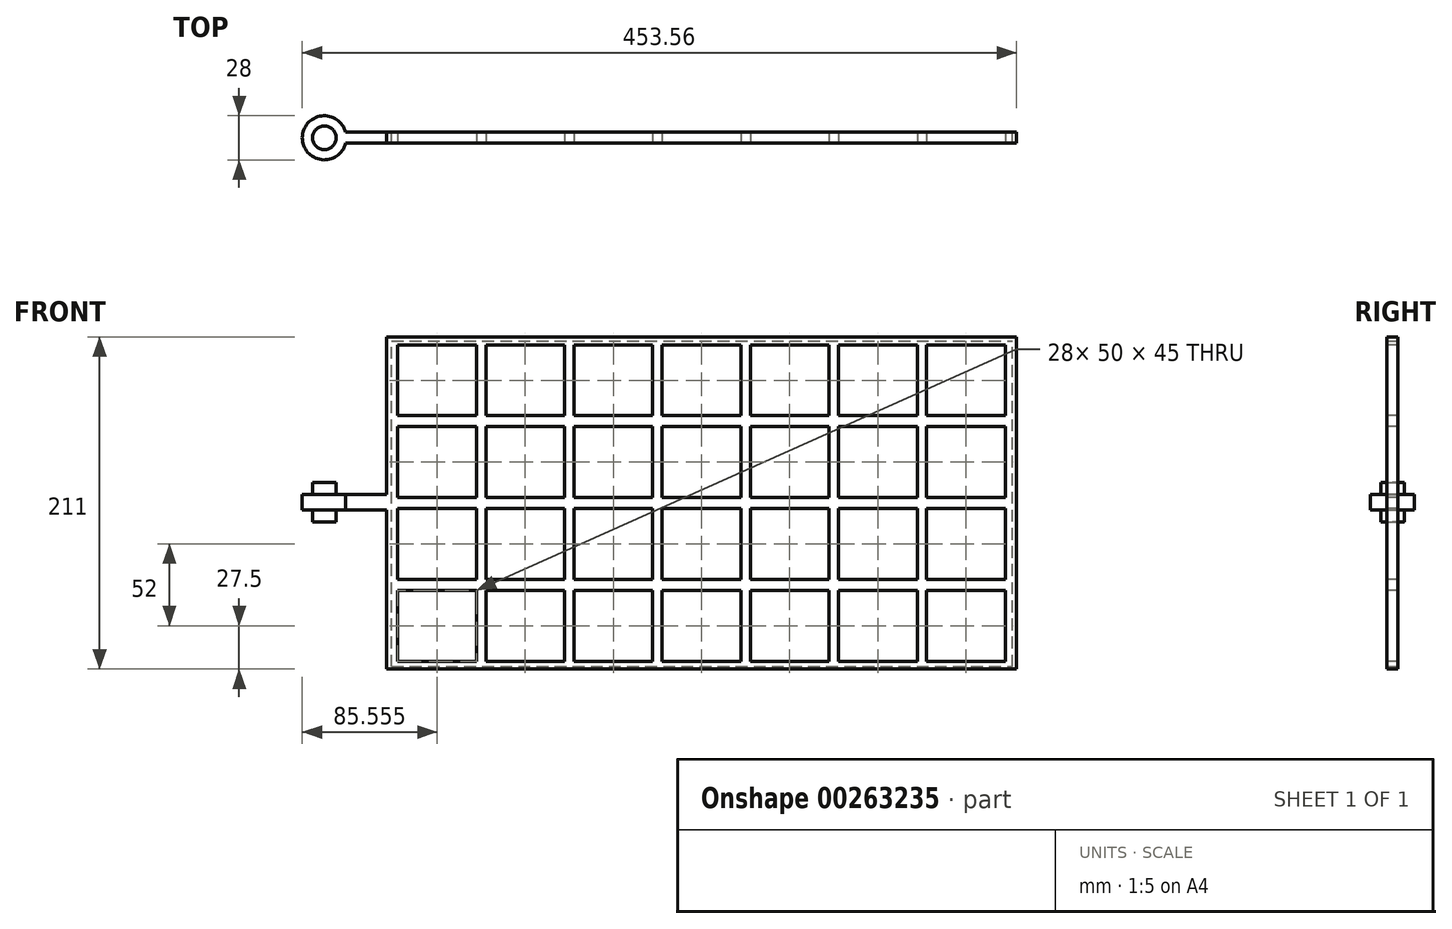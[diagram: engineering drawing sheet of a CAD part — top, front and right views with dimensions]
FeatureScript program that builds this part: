
annotation { "Feature Type Name" : "Feature", "Feature Type Description" : "" }
export const myFeature = defineFeature(function(context is Context, id is Id, definition is map)
    precondition{}
    {
        {
            var Q0;
            Q0=qCreatedBy(makeId("Top.planeOp"),FACE);
            var sketch = newSketch(context, id + "F0", { "sketchPlane" : qUnion([Q0])});
            skCircle(sketch, "E0", {"center": v(0, 0) * mm, "radius": 7.5 * mm});
            skSolve(sketch);
        }
        {
            var Q0;
            Q0 = qSketchRegion(id + "F0", true);
            extrude(context, id + "F1", {"entities" : qUnion([Q0]), "endBound" : BoundingType.SYMMETRIC, "depth" : 25 * mm});
        }
        {
            var Q0;
            Q0=qCreatedBy(makeId("Top.planeOp"),FACE);
            var sketch = newSketch(context, id + "F2", { "sketchPlane" : qUnion([Q0])});
            skArc(sketch, "E1", {"start": v(13.56, 3.5) * mm, "mid": v(-14, 0) * mm, "end": v(13.56, -3.5) * mm});
            skLineSegment(sketch, "E2", {"start": v(0, 0) * mm, "end": v(45.4, 0) * mm, "construction": true});
            skLineSegment(sketch, "E3.0", {"start": v(13.56, 3.5) * mm, "end": v(39.56, 3.5) * mm});
            skLineSegment(sketch, "E4.0", {"start": v(13.56, -3.5) * mm, "end": v(39.56, -3.5) * mm});
            skLineSegment(sketch, "E5", {"start": v(39.56, 3.5) * mm, "end": v(39.56, -3.5) * mm});
            skSolve(sketch);
        }
        {
            var Q0;
            Q0 = qSketchRegion(id + "F2", true);
            extrude(context, id + "F3", {"entities" : qUnion([Q0]), "operationType" : NewBodyOperationType.ADD, "endBound" : BoundingType.SYMMETRIC, "depth" : 10 * mm});
        }
        {
            var Q0;
            Q0=qCreatedBy(makeId("Front.planeOp"),FACE);
            var sketch = newSketch(context, id + "F4", { "sketchPlane" : qUnion([Q0])});
            skPoint(sketch, "E6", {"position": v(39.56, 0) * mm});
            skLineSegment(sketch, "E7", {"start": v(39.56, 5) * mm, "end": v(39.56, 105) * mm});
            skLineSegment(sketch, "E8", {"start": v(39.56, -5) * mm, "end": v(39.56, -106) * mm});
            skLineSegment(sketch, "E9", {"start": v(39.56, 105) * mm, "end": v(439.56, 105) * mm});
            skLineSegment(sketch, "E10", {"start": v(39.56, -106) * mm, "end": v(439.56, -106) * mm});
            skLineSegment(sketch, "E11", {"start": v(439.56, -106) * mm, "end": v(439.56, 105) * mm});
            skLineSegment(sketch, "E12", {"start": v(39.56, 5) * mm, "end": v(39.56, -5) * mm});
            skLineSegment(sketch, "E13.bottom", {"start": v(46.56, 100) * mm, "end": v(96.56, 100) * mm});
            skLineSegment(sketch, "E13.top", {"start": v(46.56, 55) * mm, "end": v(96.56, 55) * mm});
            skLineSegment(sketch, "E13.left", {"start": v(46.56, 100) * mm, "end": v(46.56, 55) * mm});
            skLineSegment(sketch, "E13.right", {"start": v(96.56, 100) * mm, "end": v(96.56, 55) * mm});
            skLineSegment(sketch, "E14.0.1.0", {"start": v(46.56, 3) * mm, "end": v(96.56, 3) * mm});
            skLineSegment(sketch, "E14.0.1.1", {"start": v(96.56, 48) * mm, "end": v(96.56, 3) * mm});
            skLineSegment(sketch, "E14.0.1.2", {"start": v(46.56, 48) * mm, "end": v(46.56, 3) * mm});
            skLineSegment(sketch, "E14.0.1.3", {"start": v(46.56, 48) * mm, "end": v(96.56, 48) * mm});
            skLineSegment(sketch, "E14.0.2.0", {"start": v(46.56, -49) * mm, "end": v(96.56, -49) * mm});
            skLineSegment(sketch, "E14.0.2.1", {"start": v(96.56, -4) * mm, "end": v(96.56, -49) * mm});
            skLineSegment(sketch, "E14.0.2.2", {"start": v(46.56, -4) * mm, "end": v(46.56, -49) * mm});
            skLineSegment(sketch, "E14.0.2.3", {"start": v(46.56, -4) * mm, "end": v(96.56, -4) * mm});
            skLineSegment(sketch, "E14.0.3.0", {"start": v(46.56, -101) * mm, "end": v(96.56, -101) * mm});
            skLineSegment(sketch, "E14.0.3.1", {"start": v(96.56, -56) * mm, "end": v(96.56, -101) * mm});
            skLineSegment(sketch, "E14.0.3.2", {"start": v(46.56, -56) * mm, "end": v(46.56, -101) * mm});
            skLineSegment(sketch, "E14.0.3.3", {"start": v(46.56, -56) * mm, "end": v(96.56, -56) * mm});
            skLineSegment(sketch, "E14.1.0.0", {"start": v(102.56, 55) * mm, "end": v(152.56, 55) * mm});
            skLineSegment(sketch, "E14.1.0.1", {"start": v(152.56, 100) * mm, "end": v(152.56, 55) * mm});
            skLineSegment(sketch, "E14.1.0.2", {"start": v(102.56, 100) * mm, "end": v(102.56, 55) * mm});
            skLineSegment(sketch, "E14.1.0.3", {"start": v(102.56, 100) * mm, "end": v(152.56, 100) * mm});
            skLineSegment(sketch, "E14.1.1.0", {"start": v(102.56, 3) * mm, "end": v(152.56, 3) * mm});
            skLineSegment(sketch, "E14.1.1.1", {"start": v(152.56, 48) * mm, "end": v(152.56, 3) * mm});
            skLineSegment(sketch, "E14.1.1.2", {"start": v(102.56, 48) * mm, "end": v(102.56, 3) * mm});
            skLineSegment(sketch, "E14.1.1.3", {"start": v(102.56, 48) * mm, "end": v(152.56, 48) * mm});
            skLineSegment(sketch, "E14.1.2.0", {"start": v(102.56, -49) * mm, "end": v(152.56, -49) * mm});
            skLineSegment(sketch, "E14.1.2.1", {"start": v(152.56, -4) * mm, "end": v(152.56, -49) * mm});
            skLineSegment(sketch, "E14.1.2.2", {"start": v(102.56, -4) * mm, "end": v(102.56, -49) * mm});
            skLineSegment(sketch, "E14.1.2.3", {"start": v(102.56, -4) * mm, "end": v(152.56, -4) * mm});
            skLineSegment(sketch, "E14.1.3.0", {"start": v(102.56, -101) * mm, "end": v(152.56, -101) * mm});
            skLineSegment(sketch, "E14.1.3.1", {"start": v(152.56, -56) * mm, "end": v(152.56, -101) * mm});
            skLineSegment(sketch, "E14.1.3.2", {"start": v(102.56, -56) * mm, "end": v(102.56, -101) * mm});
            skLineSegment(sketch, "E14.1.3.3", {"start": v(102.56, -56) * mm, "end": v(152.56, -56) * mm});
            skLineSegment(sketch, "E14.2.0.0", {"start": v(158.56, 55) * mm, "end": v(208.56, 55) * mm});
            skLineSegment(sketch, "E14.2.0.1", {"start": v(208.56, 100) * mm, "end": v(208.56, 55) * mm});
            skLineSegment(sketch, "E14.2.0.2", {"start": v(158.56, 100) * mm, "end": v(158.56, 55) * mm});
            skLineSegment(sketch, "E14.2.0.3", {"start": v(158.56, 100) * mm, "end": v(208.56, 100) * mm});
            skLineSegment(sketch, "E14.2.1.0", {"start": v(158.56, 3) * mm, "end": v(208.56, 3) * mm});
            skLineSegment(sketch, "E14.2.1.1", {"start": v(208.56, 48) * mm, "end": v(208.56, 3) * mm});
            skLineSegment(sketch, "E14.2.1.2", {"start": v(158.56, 48) * mm, "end": v(158.56, 3) * mm});
            skLineSegment(sketch, "E14.2.1.3", {"start": v(158.56, 48) * mm, "end": v(208.56, 48) * mm});
            skLineSegment(sketch, "E14.2.2.0", {"start": v(158.56, -49) * mm, "end": v(208.56, -49) * mm});
            skLineSegment(sketch, "E14.2.2.1", {"start": v(208.56, -4) * mm, "end": v(208.56, -49) * mm});
            skLineSegment(sketch, "E14.2.2.2", {"start": v(158.56, -4) * mm, "end": v(158.56, -49) * mm});
            skLineSegment(sketch, "E14.2.2.3", {"start": v(158.56, -4) * mm, "end": v(208.56, -4) * mm});
            skLineSegment(sketch, "E14.2.3.0", {"start": v(158.56, -101) * mm, "end": v(208.56, -101) * mm});
            skLineSegment(sketch, "E14.2.3.1", {"start": v(208.56, -56) * mm, "end": v(208.56, -101) * mm});
            skLineSegment(sketch, "E14.2.3.2", {"start": v(158.56, -56) * mm, "end": v(158.56, -101) * mm});
            skLineSegment(sketch, "E14.2.3.3", {"start": v(158.56, -56) * mm, "end": v(208.56, -56) * mm});
            skLineSegment(sketch, "E14.3.0.0", {"start": v(214.56, 55) * mm, "end": v(264.56, 55) * mm});
            skLineSegment(sketch, "E14.3.0.1", {"start": v(264.56, 100) * mm, "end": v(264.56, 55) * mm});
            skLineSegment(sketch, "E14.3.0.2", {"start": v(214.56, 100) * mm, "end": v(214.56, 55) * mm});
            skLineSegment(sketch, "E14.3.0.3", {"start": v(214.56, 100) * mm, "end": v(264.56, 100) * mm});
            skLineSegment(sketch, "E14.3.1.0", {"start": v(214.56, 3) * mm, "end": v(264.56, 3) * mm});
            skLineSegment(sketch, "E14.3.1.1", {"start": v(264.56, 48) * mm, "end": v(264.56, 3) * mm});
            skLineSegment(sketch, "E14.3.1.2", {"start": v(214.56, 48) * mm, "end": v(214.56, 3) * mm});
            skLineSegment(sketch, "E14.3.1.3", {"start": v(214.56, 48) * mm, "end": v(264.56, 48) * mm});
            skLineSegment(sketch, "E14.3.2.0", {"start": v(214.56, -49) * mm, "end": v(264.56, -49) * mm});
            skLineSegment(sketch, "E14.3.2.1", {"start": v(264.56, -4) * mm, "end": v(264.56, -49) * mm});
            skLineSegment(sketch, "E14.3.2.2", {"start": v(214.56, -4) * mm, "end": v(214.56, -49) * mm});
            skLineSegment(sketch, "E14.3.2.3", {"start": v(214.56, -4) * mm, "end": v(264.56, -4) * mm});
            skLineSegment(sketch, "E14.3.3.0", {"start": v(214.56, -101) * mm, "end": v(264.56, -101) * mm});
            skLineSegment(sketch, "E14.3.3.1", {"start": v(264.56, -56) * mm, "end": v(264.56, -101) * mm});
            skLineSegment(sketch, "E14.3.3.2", {"start": v(214.56, -56) * mm, "end": v(214.56, -101) * mm});
            skLineSegment(sketch, "E14.3.3.3", {"start": v(214.56, -56) * mm, "end": v(264.56, -56) * mm});
            skLineSegment(sketch, "E14.4.0.0", {"start": v(270.56, 55) * mm, "end": v(320.56, 55) * mm});
            skLineSegment(sketch, "E14.4.0.1", {"start": v(320.56, 100) * mm, "end": v(320.56, 55) * mm});
            skLineSegment(sketch, "E14.4.0.2", {"start": v(270.56, 100) * mm, "end": v(270.56, 55) * mm});
            skLineSegment(sketch, "E14.4.0.3", {"start": v(270.56, 100) * mm, "end": v(320.56, 100) * mm});
            skLineSegment(sketch, "E14.4.1.0", {"start": v(270.56, 3) * mm, "end": v(320.56, 3) * mm});
            skLineSegment(sketch, "E14.4.1.1", {"start": v(320.56, 48) * mm, "end": v(320.56, 3) * mm});
            skLineSegment(sketch, "E14.4.1.2", {"start": v(270.56, 48) * mm, "end": v(270.56, 3) * mm});
            skLineSegment(sketch, "E14.4.1.3", {"start": v(270.56, 48) * mm, "end": v(320.56, 48) * mm});
            skLineSegment(sketch, "E14.4.2.0", {"start": v(270.56, -49) * mm, "end": v(320.56, -49) * mm});
            skLineSegment(sketch, "E14.4.2.1", {"start": v(320.56, -4) * mm, "end": v(320.56, -49) * mm});
            skLineSegment(sketch, "E14.4.2.2", {"start": v(270.56, -4) * mm, "end": v(270.56, -49) * mm});
            skLineSegment(sketch, "E14.4.2.3", {"start": v(270.56, -4) * mm, "end": v(320.56, -4) * mm});
            skLineSegment(sketch, "E14.4.3.0", {"start": v(270.56, -101) * mm, "end": v(320.56, -101) * mm});
            skLineSegment(sketch, "E14.4.3.1", {"start": v(320.56, -56) * mm, "end": v(320.56, -101) * mm});
            skLineSegment(sketch, "E14.4.3.2", {"start": v(270.56, -56) * mm, "end": v(270.56, -101) * mm});
            skLineSegment(sketch, "E14.4.3.3", {"start": v(270.56, -56) * mm, "end": v(320.56, -56) * mm});
            skLineSegment(sketch, "E14.5.0.0", {"start": v(326.56, 55) * mm, "end": v(376.56, 55) * mm});
            skLineSegment(sketch, "E14.5.0.1", {"start": v(376.56, 100) * mm, "end": v(376.56, 55) * mm});
            skLineSegment(sketch, "E14.5.0.2", {"start": v(326.56, 100) * mm, "end": v(326.56, 55) * mm});
            skLineSegment(sketch, "E14.5.0.3", {"start": v(326.56, 100) * mm, "end": v(376.56, 100) * mm});
            skLineSegment(sketch, "E14.5.1.0", {"start": v(326.56, 3) * mm, "end": v(376.56, 3) * mm});
            skLineSegment(sketch, "E14.5.1.1", {"start": v(376.56, 48) * mm, "end": v(376.56, 3) * mm});
            skLineSegment(sketch, "E14.5.1.2", {"start": v(326.56, 48) * mm, "end": v(326.56, 3) * mm});
            skLineSegment(sketch, "E14.5.1.3", {"start": v(326.56, 48) * mm, "end": v(376.56, 48) * mm});
            skLineSegment(sketch, "E14.5.2.0", {"start": v(326.56, -49) * mm, "end": v(376.56, -49) * mm});
            skLineSegment(sketch, "E14.5.2.1", {"start": v(376.56, -4) * mm, "end": v(376.56, -49) * mm});
            skLineSegment(sketch, "E14.5.2.2", {"start": v(326.56, -4) * mm, "end": v(326.56, -49) * mm});
            skLineSegment(sketch, "E14.5.2.3", {"start": v(326.56, -4) * mm, "end": v(376.56, -4) * mm});
            skLineSegment(sketch, "E14.5.3.0", {"start": v(326.56, -101) * mm, "end": v(376.56, -101) * mm});
            skLineSegment(sketch, "E14.5.3.1", {"start": v(376.56, -56) * mm, "end": v(376.56, -101) * mm});
            skLineSegment(sketch, "E14.5.3.2", {"start": v(326.56, -56) * mm, "end": v(326.56, -101) * mm});
            skLineSegment(sketch, "E14.5.3.3", {"start": v(326.56, -56) * mm, "end": v(376.56, -56) * mm});
            skLineSegment(sketch, "E14.6.0.0", {"start": v(382.56, 55) * mm, "end": v(432.56, 55) * mm});
            skLineSegment(sketch, "E14.6.0.1", {"start": v(432.56, 100) * mm, "end": v(432.56, 55) * mm});
            skLineSegment(sketch, "E14.6.0.2", {"start": v(382.56, 100) * mm, "end": v(382.56, 55) * mm});
            skLineSegment(sketch, "E14.6.0.3", {"start": v(382.56, 100) * mm, "end": v(432.56, 100) * mm});
            skLineSegment(sketch, "E14.6.1.0", {"start": v(382.56, 3) * mm, "end": v(432.56, 3) * mm});
            skLineSegment(sketch, "E14.6.1.1", {"start": v(432.56, 48) * mm, "end": v(432.56, 3) * mm});
            skLineSegment(sketch, "E14.6.1.2", {"start": v(382.56, 48) * mm, "end": v(382.56, 3) * mm});
            skLineSegment(sketch, "E14.6.1.3", {"start": v(382.56, 48) * mm, "end": v(432.56, 48) * mm});
            skLineSegment(sketch, "E14.6.2.0", {"start": v(382.56, -49) * mm, "end": v(432.56, -49) * mm});
            skLineSegment(sketch, "E14.6.2.1", {"start": v(432.56, -4) * mm, "end": v(432.56, -49) * mm});
            skLineSegment(sketch, "E14.6.2.2", {"start": v(382.56, -4) * mm, "end": v(382.56, -49) * mm});
            skLineSegment(sketch, "E14.6.2.3", {"start": v(382.56, -4) * mm, "end": v(432.56, -4) * mm});
            skLineSegment(sketch, "E14.6.3.0", {"start": v(382.56, -101) * mm, "end": v(432.56, -101) * mm});
            skLineSegment(sketch, "E14.6.3.1", {"start": v(432.56, -56) * mm, "end": v(432.56, -101) * mm});
            skLineSegment(sketch, "E14.6.3.2", {"start": v(382.56, -56) * mm, "end": v(382.56, -101) * mm});
            skLineSegment(sketch, "E14.6.3.3", {"start": v(382.56, -56) * mm, "end": v(432.56, -56) * mm});
            skLineSegment(sketch, "E14.direction1", {"start": v(46.56, 55) * mm, "end": v(102.56, 55) * mm, "construction": true});
            skLineSegment(sketch, "E14.direction2", {"start": v(46.56, 55) * mm, "end": v(46.56, 3) * mm, "construction": true});
            skSolve(sketch);
        }
        {
            var Q0;
            Q0 = qSketchRegion(id + "F4", true);
            var Q1;
            Q1=makeQuery(id+"F3.opExtrude","SWEPT_FACE",FACE,{"disambiguationData":[OSD([sQuery(id+"F2.wireOp",EDGE,"E4.0")])]});
            extrude(context, id + "F5", {"entities" : qUnion([Q0]), "operationType" : NewBodyOperationType.ADD, "endBound" : BoundingType.SYMMETRIC, "oppositeDirection" : true, "endBoundEntityFace" : qUnion([Q1]), "depth" : 7 * mm});
        }
        {
            var Q0;
            Q0=qCreatedBy(makeId("Front.planeOp"),FACE);
            var sketch = newSketch(context, id + "F6", { "sketchPlane" : qUnion([Q0])});
            skLineSegment(sketch, "E15.bottom", {"start": v(42.74, -104.33) * mm, "end": v(437.03, -104.33) * mm});
            skLineSegment(sketch, "E15.top", {"start": v(42.74, 102.27) * mm, "end": v(437.03, 102.27) * mm});
            skLineSegment(sketch, "E15.left", {"start": v(42.74, -104.33) * mm, "end": v(42.74, 102.27) * mm});
            skLineSegment(sketch, "E15.right", {"start": v(437.03, -104.33) * mm, "end": v(437.03, 102.27) * mm});
            skSolve(sketch);
        }
        {
            var Q0;
            Q0 = qSketchRegion(id + "F6", true);
            extrude(context, id + "F7", {"entities" : qUnion([Q0]), "endBound" : BoundingType.SYMMETRIC, "depth" : 6.5 * mm});
        }
    });
